# Revit family: Gira_543300
name_source: partatom
category: Elektroinstallationen
revit_build: Autodesk Revit 2017 (Build: 20160225_1515(x64)
units: mm (PartAtom-declared; Revit-internal decimal feet)

## family parameters
Basisbauteil = Fläche
Beim Laden mit Abzugskörper schneiden = Nein
Bemaßung runder Anschluss = Durchmesser verwenden
Beschriftungsausrichtung beibehalten = Nein
Gemeinsam genutzt = Nein
Raumberechnungspunkt = Nein
Teiletyp = Normal

## types (1)
- Funk Schalt-/Tastaktor 1f REG Gira eNet
    Andere Bussysteme = eNet
    Anzahl der Eingänge = 0
    Anzahl der binären Eingänge = 1
    App-Steuerung über Bluetooth = Nein
    BIM = https://media.stage.bim.site X1 REG KNX.rfa
    BIMSITE_PRODUCT_ID = 09d5c4e62c6d905a1ec09bf9e37d86a6310b734c
    Beschreibung = eNet Funk Schalt- bzw. Tastaktor 1fach  REG Merkmale: Mit eNet Server einstellbar::  Vollverschlüsselte Funkübertragung (AES-CCM) ab eNet Server Software Version 2.0.  Bediensperren.  Update der Gerätesoftware.  Der eNet Funk Schalt- bzw. Funk Tastaktor empfängt über eine Datenleitung vom eNet Funk Empfangsmodul oder eNet Server Telegramme zum Schalten von Beleuchtungen.  Betriebsarten: Schaltaktor oder Tastaktor.  Statusrückmeldung an eNet Funksender.  Szenenbetrieb.  Betriebsart Tasten: Relaiskontakt bleibt so lange geschlossen wie Telegramme empfangen werden (max. 60 Sekunden). Mit eNet Server einstellbar::  Blinkfunktion.  Nachlaufzeit.  Ein- bzw. Ausschaltverzögerung.  Abschaltvorwarnung.  Minimale Schaltwiederholzeit.  Dauer-Ein, Dauer-Aus.  Hinweise :  Zum Betrieb dieses Reiheneinbaugeräts wird ein eNet Funk Empfangsmodul oder ein eNet Server benötigt.
    Breite in Teilungseinheiten = 2
    Bussystem Funkbus = Ja
    Bussystem KNX = Nein
    Bussystem KNX-Funk = Nein
    Bussystem LON = Nein
    Bussystem Powernet = Nein
    Datenblatt = https://media.stage.bim.site
    Datenblatt 1 = https://media.stage.bim.site
    Dimmung Phasenabschnitt = Nein
    Dimmung Phasenanschnitt = Nein
    Funk bidirektional = Nein
    Funktion Schalten = Nein
    GTIN = 4010337774273
    Geeignet für C-Last = Nein
    HAN = 543300
    Halogenfrei = Nein
    HeinzeBIM = https://www.heinze.de
    Hersteller = Gira
    Kosten = 0 $
    Lichtwertspeicher = Nein
    Max. Anzahl der Jalousieausgänge = 0
    Max. Anzahl der Schaltausgänge = 1
    Max. Schaltleistung [Voltampere] = 2300
    Mit Beschriftungsfeld = Nein
    Mit Busankopplung = Nein
    Mit LED-Anzeige = Nein
    Modulare Erweiterungsmöglichkeit = Nein
    Montageart = REG
    Nebenstelleneingang = Nein
    Produktseite = https://media.stage.bim.site
    Schutzart (IP) = IP20
    Seriendimmer = Nein
    Transparent = Nein
    Typname = Funk Schalt-/Tastaktor 1f REG Gira eNet
    URL = https://www.gira.de
    Verschiedene Phasen anschließbar = Nein
    Verwendbar mit Bewegungsmelder = Nein
    Verwendbar mit Funktaste = Nein
    Verwendbar mit IR-Taste = Nein
    Verwendbar mit Präsenzmelder = Nein
    Verwendbar mit Taste = Nein
    Verwendbar mit Zeitschalter/Timer = Nein
    Vor Ort-/Handbedienung = Nein
    Vorgabe-Ansicht = 1219 mm

## geometry (parser evidence)
native form markers: Sweep x2
no freeform markers — native parametric forms only
